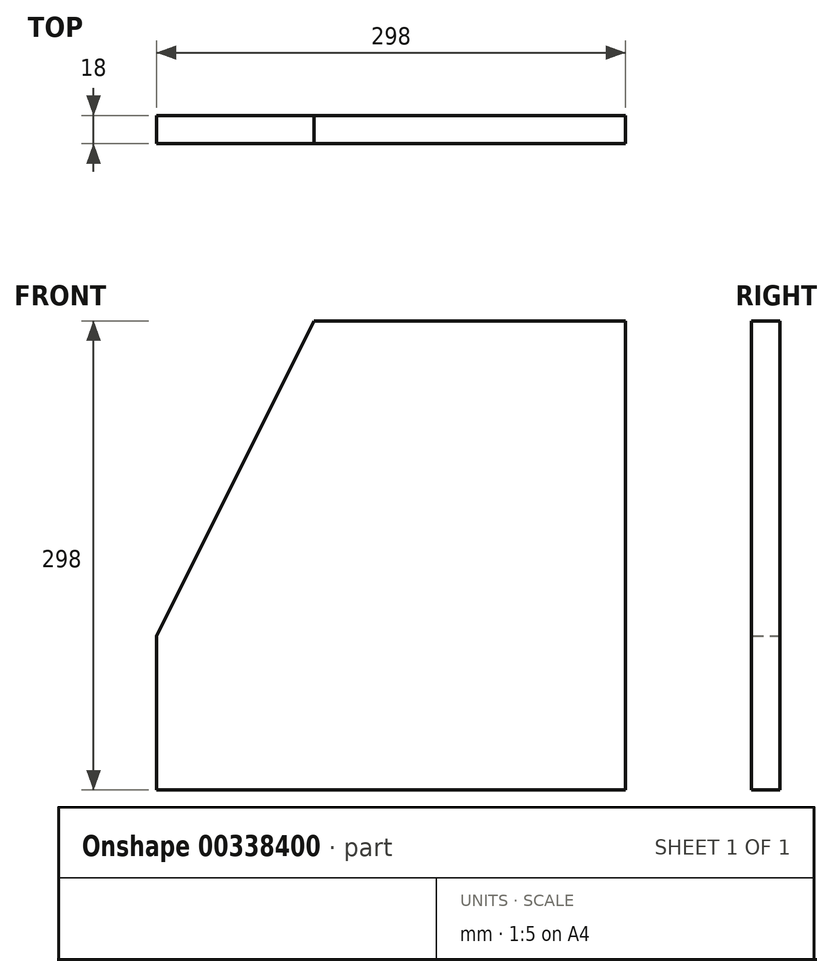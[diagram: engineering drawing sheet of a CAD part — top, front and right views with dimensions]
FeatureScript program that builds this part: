
annotation { "Feature Type Name" : "Feature", "Feature Type Description" : "" }
export const myFeature = defineFeature(function(context is Context, id is Id, definition is map)
    precondition{}
    {
        {
            var Q0;
            Q0=qCreatedBy(makeId("Front.planeOp"),FACE);
            var sketch = newSketch(context, id + "F0", { "sketchPlane" : qUnion([Q0])});
            skLineSegment(sketch, "E0.bottom", {"start": v(-99, -149) * mm, "end": v(99, -149) * mm});
            skLineSegment(sketch, "E0.top", {"start": v(-99, 149) * mm, "end": v(99, 149) * mm});
            skLineSegment(sketch, "E0.left", {"start": v(-99, -51) * mm, "end": v(-99, 149) * mm});
            skLineSegment(sketch, "E0.right", {"start": v(99, -51) * mm, "end": v(99, 149) * mm});
            skPoint(sketch, "E0.middle", {"position": v(0, 0) * mm});
            skLineSegment(sketch, "E1.bottom", {"start": v(-99, -149) * mm, "end": v(-199, -149) * mm});
            skLineSegment(sketch, "E1.top", {"start": v(-99, -51) * mm, "end": v(-199, -51) * mm});
            skLineSegment(sketch, "E1.right", {"start": v(-199, -149) * mm, "end": v(-199, -51) * mm});
            skLineSegment(sketch, "E2", {"start": v(-199, -51) * mm, "end": v(-99, 149) * mm});
            skLineSegment(sketch, "E3", {"start": v(99, -51) * mm, "end": v(99, -149) * mm});
            skSolve(sketch);
        }
        {
            var Q0;
            Q0=makeQuery(id+"F0.imprint","IMPRINT",FACE,{"disambiguationData":[TD([[makeQuery(id+"F0.imprint","IMPRINT",EDGE,{"derivedFrom":sQuery(id+"F0.wireOp",EDGE,"E0.right")}),-1.0]])]});
            var Q1;
            Q1=makeQuery(id+"F0.imprint","IMPRINT",FACE,{"disambiguationData":[TD([[makeQuery(id+"F0.imprint","IMPRINT",EDGE,{"derivedFrom":sQuery(id+"F0.wireOp",EDGE,"E0.bottom")}),1.0]])]});
            var Q2;
            Q2=makeQuery(id+"F0.imprint","IMPRINT",FACE,{"disambiguationData":[TD([[makeQuery(id+"F0.imprint","IMPRINT",EDGE,{"derivedFrom":sQuery(id+"F0.wireOp",EDGE,"E0.left")}),1.0]])]});
            extrude(context, id + "F1", {"entities" : qUnion([Q0, Q1, Q2]), "depth" : 18 * mm});
        }
    });
